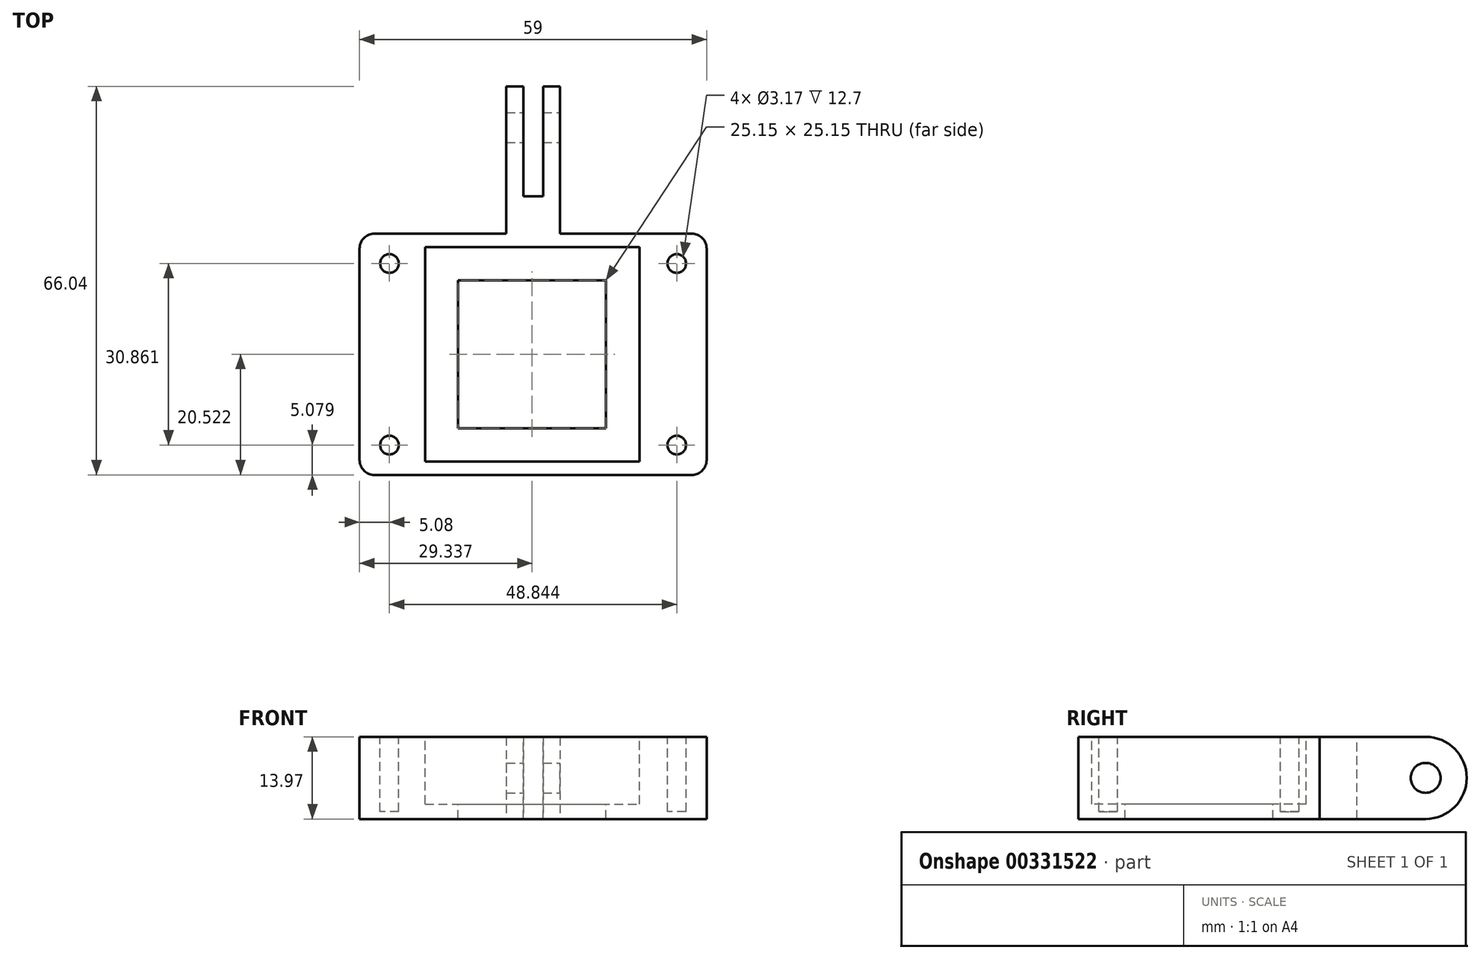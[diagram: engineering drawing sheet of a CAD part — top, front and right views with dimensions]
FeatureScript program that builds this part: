
annotation { "Feature Type Name" : "Feature", "Feature Type Description" : "" }
export const myFeature = defineFeature(function(context is Context, id is Id, definition is map)
    precondition{}
    {
        {
            var Q0;
            Q0=qCreatedBy(makeId("Top.planeOp"),FACE);
            var sketch = newSketch(context, id + "F0", { "sketchPlane" : qUnion([Q0])});
            skLineSegment(sketch, "E0.bottom", {"start": v(-25.4, 25.4) * mm, "end": v(33.6, 25.4) * mm});
            skLineSegment(sketch, "E0.top", {"start": v(-25.4, -15.62) * mm, "end": v(33.6, -15.62) * mm});
            skLineSegment(sketch, "E0.left", {"start": v(-25.4, 25.4) * mm, "end": v(-25.4, -15.62) * mm});
            skLineSegment(sketch, "E0.right", {"start": v(33.6, 25.4) * mm, "end": v(33.6, -15.62) * mm});
            skSolve(sketch);
        }
        {
            var Q0;
            Q0=makeQuery(id+"F0.imprint","IMPRINT",FACE,{"disambiguationData":[TD([[makeQuery(id+"F0.imprint","IMPRINT",EDGE,{"derivedFrom":sQuery(id+"F0.wireOp",EDGE,"E0.bottom")}),-1.0]])]});
            extrude(context, id + "F1", {"entities" : qUnion([Q0]), "depth" : 13.97 * mm});
        }
        {
            var Q0;
            Q0=makeQuery(id+"F1.opExtrude","SWEPT_EDGE",EDGE,{"disambiguationData":[OSD([sQuery(id+"F0.wireOp",EDGE,"E0.bottom"),sQuery(id+"F0.wireOp",EDGE,"E0.left")])]});
            var Q1;
            Q1=makeQuery(id+"F1.opExtrude","SWEPT_EDGE",EDGE,{"disambiguationData":[OSD([sQuery(id+"F0.wireOp",EDGE,"E0.bottom"),sQuery(id+"F0.wireOp",EDGE,"E0.right")])]});
            var Q2;
            Q2=makeQuery(id+"F1.opExtrude","SWEPT_EDGE",EDGE,{"disambiguationData":[OSD([sQuery(id+"F0.wireOp",EDGE,"E0.top"),sQuery(id+"F0.wireOp",EDGE,"E0.right")])]});
            var Q3;
            Q3=makeQuery(id+"F1.opExtrude","SWEPT_EDGE",EDGE,{"disambiguationData":[OSD([sQuery(id+"F0.wireOp",EDGE,"E0.top"),sQuery(id+"F0.wireOp",EDGE,"E0.left")])]});
            fillet(context, id + "F2", {"entities" : qUnion([Q0, Q1, Q2, Q3]), "radius" : 2.54 * mm, "tangentPropagation" : true, "allowEdgeOverflow" : false});
        }
        {
            var Q0;
            Q0=makeQuery(id+"F1.opExtrude","CAP_FACE",FACE,{"disambiguationData":[OSD([sQuery(id+"F0.wireOp",EDGE,"E0.bottom"),sQuery(id+"F0.wireOp",EDGE,"E0.top"),sQuery(id+"F0.wireOp",EDGE,"E0.left"),sQuery(id+"F0.wireOp",EDGE,"E0.right")])],"isStart":false});
            var sketch = newSketch(context, id + "F3", { "sketchPlane" : qUnion([Q0])});
            skLineSegment(sketch, "E1.bottom", {"start": v(-14.27, 23.11) * mm, "end": v(22.17, 23.11) * mm});
            skLineSegment(sketch, "E1.top", {"start": v(-14.27, -13.34) * mm, "end": v(22.17, -13.33) * mm});
            skLineSegment(sketch, "E1.left", {"start": v(-14.27, 23.11) * mm, "end": v(-14.27, -13.34) * mm});
            skLineSegment(sketch, "E1.right", {"start": v(22.17, 23.11) * mm, "end": v(22.17, -13.33) * mm});
            skSolve(sketch);
        }
        {
            var Q0;
            Q0=makeQuery(id+"F3.imprint","IMPRINT",FACE,{"disambiguationData":[TD([[makeQuery(id+"F3.imprint","IMPRINT",EDGE,{"derivedFrom":sQuery(id+"F3.wireOp",EDGE,"E1.bottom")}),-1.0]])]});
            extrude(context, id + "F4", {"entities" : qUnion([Q0]), "operationType" : NewBodyOperationType.REMOVE, "oppositeDirection" : true, "depth" : 11.43 * mm});
        }
        {
            var Q0;
            Q0=makeQuery(id+"F4.boolean.opBoolean","COPY",FACE,{"derivedFrom":makeQuery(id+"F4.opExtrude","CAP_FACE",FACE,{"disambiguationData":[OSD([sQuery(id+"F3.wireOp",EDGE,"E1.bottom"),sQuery(id+"F3.wireOp",EDGE,"E1.top"),sQuery(id+"F3.wireOp",EDGE,"E1.left"),sQuery(id+"F3.wireOp",EDGE,"E1.right")])],"isStart":false})});
            var sketch = newSketch(context, id + "F5", { "sketchPlane" : qUnion([Q0])});
            skLineSegment(sketch, "E2.bottom", {"start": v(-8.64, 17.48) * mm, "end": v(16.51, 17.48) * mm});
            skLineSegment(sketch, "E2.top", {"start": v(-8.64, -7.67) * mm, "end": v(16.51, -7.67) * mm});
            skLineSegment(sketch, "E2.left", {"start": v(-8.64, 17.48) * mm, "end": v(-8.64, -7.67) * mm});
            skLineSegment(sketch, "E2.right", {"start": v(16.51, 17.48) * mm, "end": v(16.51, -7.67) * mm});
            skSolve(sketch);
        }
        {
            var Q0;
            Q0=makeQuery(id+"F5.imprint","IMPRINT",FACE,{"disambiguationData":[TD([[makeQuery(id+"F5.imprint","IMPRINT",EDGE,{"derivedFrom":sQuery(id+"F5.wireOp",EDGE,"E2.bottom")}),-1.0]])]});
            extrude(context, id + "F6", {"entities" : qUnion([Q0]), "operationType" : NewBodyOperationType.REMOVE, "endBound" : BoundingType.THROUGH_ALL, "oppositeDirection" : true, "depth" : 25.4 * mm});
        }
        {
            var Q0;
            Q0=makeQuery(id+"F1.opExtrude","CAP_FACE",FACE,{"disambiguationData":[OSD([sQuery(id+"F0.wireOp",EDGE,"E0.bottom"),sQuery(id+"F0.wireOp",EDGE,"E0.top"),sQuery(id+"F0.wireOp",EDGE,"E0.left"),sQuery(id+"F0.wireOp",EDGE,"E0.right")])],"isStart":false});
            var sketch = newSketch(context, id + "F7", { "sketchPlane" : qUnion([Q0])});
            skCircle(sketch, "E3", {"center": v(-20.32, 20.32) * mm, "radius": 1.59 * mm});
            skCircle(sketch, "E4", {"center": v(-20.32, -10.54) * mm, "radius": 1.59 * mm});
            skCircle(sketch, "E5", {"center": v(28.52, 20.32) * mm, "radius": 1.59 * mm});
            skCircle(sketch, "E6", {"center": v(28.52, -10.54) * mm, "radius": 1.59 * mm});
            skSolve(sketch);
        }
        {
            var Q0;
            Q0 = qSketchRegion(id + "F7", true);
            extrude(context, id + "F8", {"entities" : qUnion([Q0]), "operationType" : NewBodyOperationType.REMOVE, "oppositeDirection" : true, "depth" : 12.7 * mm});
        }
        {
            var Q0;
            Q0=makeQuery(id+"F1.opExtrude","SWEPT_FACE",FACE,{"disambiguationData":[OSD([sQuery(id+"F0.wireOp",EDGE,"E0.bottom")])]});
            var sketch = newSketch(context, id + "F9", { "sketchPlane" : qUnion([Q0])});
            skLineSegment(sketch, "E7.bottom", {"start": v(-8.69, 13.97) * mm, "end": v(0.46, 13.97) * mm});
            skLineSegment(sketch, "E7.top", {"start": v(-8.69, 0) * mm, "end": v(0.46, 0) * mm});
            skLineSegment(sketch, "E7.left", {"start": v(-8.69, 13.97) * mm, "end": v(-8.69, 0) * mm});
            skLineSegment(sketch, "E7.right", {"start": v(0.46, 13.97) * mm, "end": v(0.46, 0) * mm});
            skSolve(sketch);
        }
        {
            var Q0;
            Q0 = qSketchRegion(id + "F9", true);
            extrude(context, id + "F10", {"entities" : qUnion([Q0]), "operationType" : NewBodyOperationType.ADD, "depth" : 25.02 * mm, "offsetDistance" : 25.4 * mm});
        }
        {
            var Q0;
            Q0=makeQuery(id+"F10.opExtrude","CAP_EDGE",EDGE,{"disambiguationData":[OSD([sQuery(id+"F9.wireOp",EDGE,"E7.bottom")])],"isStart":false});
            var Q1;
            Q1=makeQuery(id+"F10.opExtrude","CAP_EDGE",EDGE,{"disambiguationData":[OSD([sQuery(id+"F9.wireOp",EDGE,"E7.top")])],"isStart":false});
            fillet(context, id + "F11", {"entities" : qUnion([Q0, Q1]), "radius" : 7 * mm, "tangentPropagation" : true, "allowEdgeOverflow" : false});
        }
        {
            var Q0;
            Q0=makeQuery(id+"F10.boolean.opBoolean","MERGE",FACE,{"derivedFrom":[makeQuery(id+"F1.opExtrude","CAP_FACE",FACE,{"disambiguationData":[OSD([sQuery(id+"F0.wireOp",EDGE,"E0.bottom"),sQuery(id+"F0.wireOp",EDGE,"E0.top"),sQuery(id+"F0.wireOp",EDGE,"E0.left"),sQuery(id+"F0.wireOp",EDGE,"E0.right")])],"isStart":false}),makeQuery(id+"F10.opExtrude","SWEPT_FACE",FACE,{"disambiguationData":[OSD([sQuery(id+"F9.wireOp",EDGE,"E7.bottom")])]})]});
            var sketch = newSketch(context, id + "F12", { "sketchPlane" : qUnion([Q0])});
            skLineSegment(sketch, "E8.bottom", {"start": v(2.44, 53.98) * mm, "end": v(5.8, 53.98) * mm});
            skLineSegment(sketch, "E8.top", {"start": v(2.44, 31.75) * mm, "end": v(5.8, 31.75) * mm});
            skLineSegment(sketch, "E8.left", {"start": v(2.44, 53.98) * mm, "end": v(2.44, 31.75) * mm});
            skLineSegment(sketch, "E8.right", {"start": v(5.8, 53.98) * mm, "end": v(5.8, 31.75) * mm});
            skSolve(sketch);
        }
        {
            var Q0;
            Q0 = qSketchRegion(id + "F12", true);
            extrude(context, id + "F13", {"entities" : qUnion([Q0]), "operationType" : NewBodyOperationType.REMOVE, "endBound" : BoundingType.THROUGH_ALL, "oppositeDirection" : true, "depth" : 25.4 * mm, "offsetDistance" : 25.4 * mm});
        }
        {
            var Q0;
            Q0=makeQuery(id+"F10.opExtrude","SWEPT_FACE",FACE,{"disambiguationData":[OSD([sQuery(id+"F9.wireOp",EDGE,"E7.left")])]});
            var sketch = newSketch(context, id + "F14", { "sketchPlane" : qUnion([Q0])});
            skCircle(sketch, "E9", {"center": v(43.43, 6.99) * mm, "radius": 2.54 * mm});
            skSolve(sketch);
        }
        {
            var Q0;
            Q0 = qSketchRegion(id + "F14", true);
            extrude(context, id + "F15", {"entities" : qUnion([Q0]), "operationType" : NewBodyOperationType.REMOVE, "endBound" : BoundingType.THROUGH_ALL, "oppositeDirection" : true, "depth" : 25.4 * mm, "offsetDistance" : 25.4 * mm});
        }
    });
